# Revit family: QF_MACOM_CB09E-DA
name_source: partatom
category: Equipamento especial
units: mm (PartAtom-declared; Revit-internal decimal feet)

## family parameters
Com base no plano de trabalho = Não
Compartilhado = Não
Corte com vazios quando carregada = Não
Cota do conector redondo = Utilizar diâmetro
Número OmniClass = 23.40.40.14.17.11
Ponto de cálculo do ambiente = Não
Sempre na vertical = Sim
Tipo de parte = Normal
Título OmniClass = Cookers, Ovens, Stoves

## types (2) — shared parameters
Depth = 686,000 mm
Descrição = CHAR BROILER EXPORTACAO MACOM 915, DUPLO GAS
Elevação padrão = 0,000 mm
Fabricante = MACOM
Gas Connection Height = 60,000 mm
Gas Size = 3/4"
Height = 395,000 mm
Modelo = CB09E-DA
Number of Burners = 7
Show Clearances = Sim
URL = https://www.acosmacom.com.br
Volume = 0,25 m³
Weight = 74,00 kg
Width = 915,000 mm

## per-type parameters (varying)
| type | Gas Consumption GLP | Gas Consumption GN | Gas Input GLP | Gas Input GN | Gas Pressure |
| CB09E-G | 2,61 Kg/h | 0 m³/h | 119015 Btu/h |  | 0,03 bar |
| CB09E-N |  | 3 m³/h | 0 Btu/h | 30015 Kcal/h | 0,02 bar |

## geometry (parser evidence)
native form markers: Sweep x5
no freeform markers — native parametric forms only
